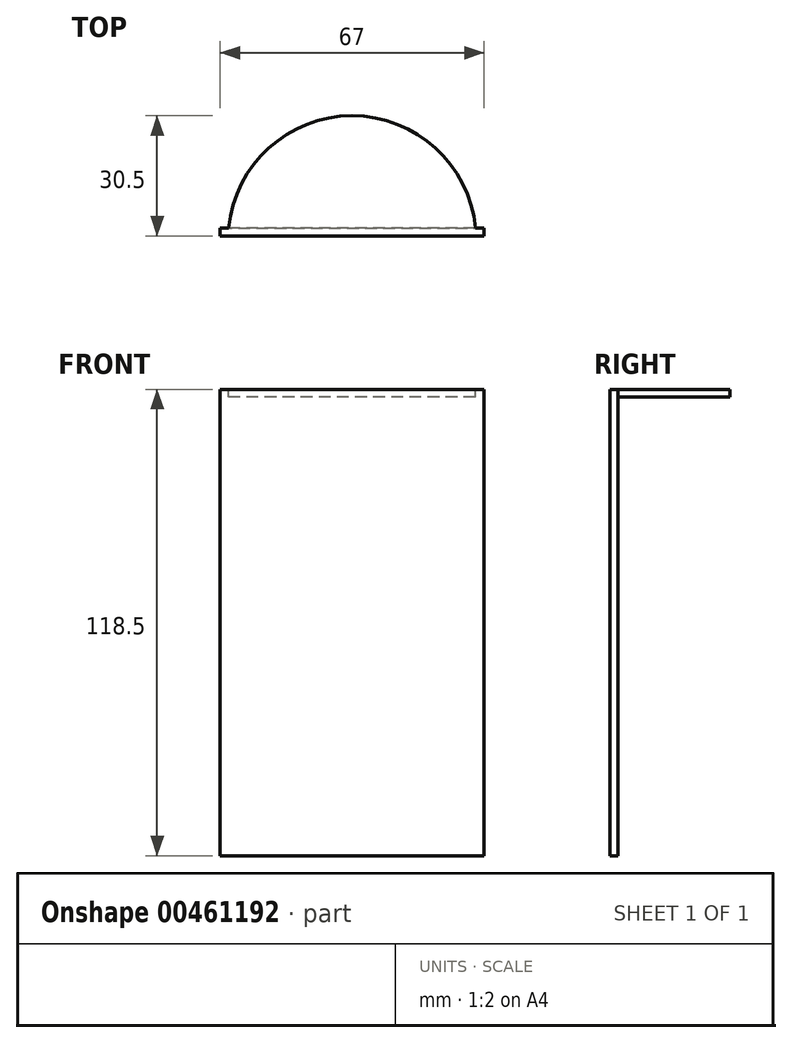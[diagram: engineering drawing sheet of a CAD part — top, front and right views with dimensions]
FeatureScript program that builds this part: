
annotation { "Feature Type Name" : "Feature", "Feature Type Description" : "" }
export const myFeature = defineFeature(function(context is Context, id is Id, definition is map)
    precondition{}
    {
        {
            var Q0;
            Q0=qCreatedBy(makeId("Front.planeOp"),FACE);
            var sketch = newSketch(context, id + "F0", { "sketchPlane" : qUnion([Q0])});
            skLineSegment(sketch, "E0.bottom", {"start": v(0, 0) * mm, "end": v(67, 0) * mm});
            skLineSegment(sketch, "E0.top", {"start": v(0, 118.5) * mm, "end": v(67, 118.5) * mm});
            skLineSegment(sketch, "E0.left", {"start": v(0, 0) * mm, "end": v(0, 118.5) * mm});
            skLineSegment(sketch, "E0.right", {"start": v(67, 0) * mm, "end": v(67, 118.5) * mm});
            skSolve(sketch);
        }
        {
            var Q0;
            Q0=makeQuery(id+"F0.imprint","IMPRINT",FACE,{"disambiguationData":[TD([[makeQuery(id+"F0.imprint","IMPRINT",EDGE,{"derivedFrom":sQuery(id+"F0.wireOp",EDGE,"E0.bottom")}),1.0]])]});
            extrude(context, id + "F1", {"entities" : qUnion([Q0]), "depth" : 2 * mm});
        }
        {
            var Q0;
            Q0=makeQuery(id+"F1.opExtrude","SWEPT_FACE",FACE,{"disambiguationData":[OSD([sQuery(id+"F0.wireOp",EDGE,"E0.top")])]});
            var sketch = newSketch(context, id + "F2", { "sketchPlane" : qUnion([Q0])});
            skCircle(sketch, "E1", {"center": v(33.5, -3) * mm, "radius": 31.5 * mm});
            skPoint(sketch, "E1.first.point", {"position": v(64.86, 0) * mm});
            skPoint(sketch, "E1.second.point", {"position": v(2.14, 0) * mm});
            skPoint(sketch, "E1.third.point", {"position": v(33.5, -34.5) * mm});
            skPoint(sketch, "E1.third.point.positionSnap0", {"position": v(33.5, 0) * mm});
            skSolve(sketch);
        }
        {
            var Q0;
            {var subQ0=sQuery(id+"F2.wireOp",EDGE,"E1");var subQ1=sQuery(id+"F0.wireOp",EDGE,"E0.top");var subQ2=makeQuery(id+"F1.opExtrude","CAP_EDGE",EDGE,{"disambiguationData":[OSD([subQ1])],"isStart":true});var subQ3=makeQuery(id+"F2.imprint","INTERSECT",VERTEX,{"disambiguationData":[OD(0.0)],"derivedFrom":[subQ2,subQ0]});Q0=makeQuery(id+"F2.imprint","IMPRINT",FACE,{"disambiguationData":[TD([[makeQuery(id+"F2.imprint","IMPRINT",EDGE,{"disambiguationData":[TD([[subQ3,1.0]])],"derivedFrom":subQ0}),1.0]])]});}
            var Q1;
            {var subQ0=sQuery(id+"F2.wireOp",EDGE,"E1");var subQ1=makeQuery(id+"F1.opExtrude","CAP_EDGE",EDGE,{"disambiguationData":[OSD([sQuery(id+"F0.wireOp",EDGE,"E0.top")])],"isStart":true});var subQ2=makeQuery(id+"F2.imprint","INTERSECT",VERTEX,{"disambiguationData":[OD(0.0)],"derivedFrom":[subQ1,subQ0]});Q1=makeQuery(id+"F2.imprint","IMPRINT",FACE,{"disambiguationData":[TD([[makeQuery(id+"F2.imprint","IMPRINT",EDGE,{"disambiguationData":[TD([[subQ2,-1.0]])],"derivedFrom":subQ0}),1.0]])]});}
            extrude(context, id + "F3", {"entities" : qUnion([Q0, Q1]), "operationType" : NewBodyOperationType.ADD, "oppositeDirection" : true, "depth" : 2 * mm});
        }
    });
